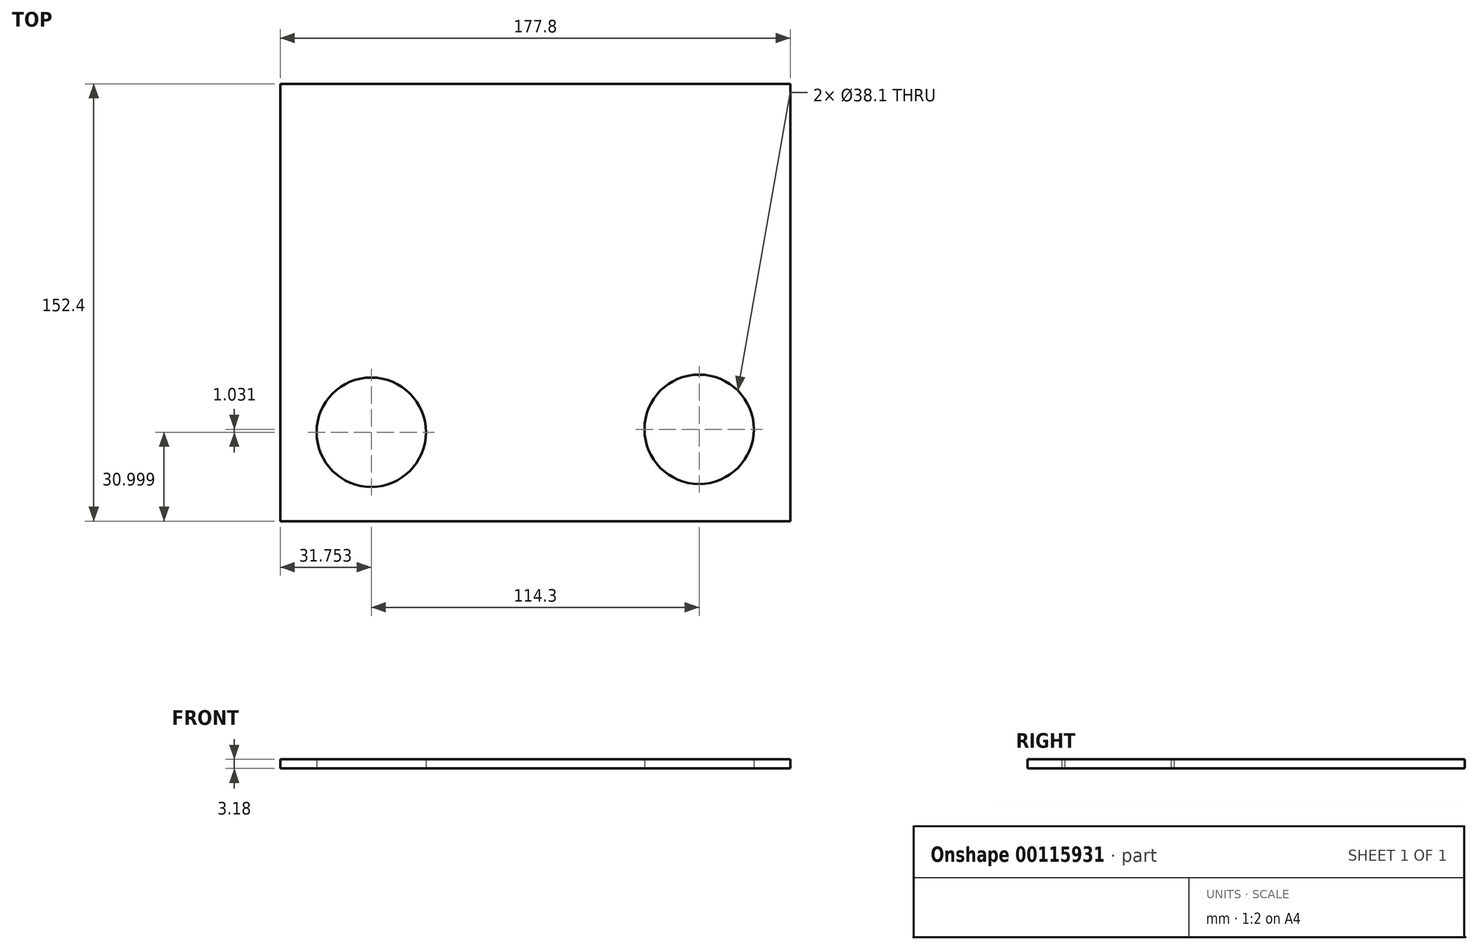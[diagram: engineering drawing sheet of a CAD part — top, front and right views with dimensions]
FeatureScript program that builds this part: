
annotation { "Feature Type Name" : "Feature", "Feature Type Description" : "" }
export const myFeature = defineFeature(function(context is Context, id is Id, definition is map)
    precondition{}
    {
        {
            var Q0;
            Q0=qCreatedBy(makeId("Top.planeOp"),FACE);
            var sketch = newSketch(context, id + "F0", { "sketchPlane" : qUnion([Q0])});
            skLineSegment(sketch, "E0.bottom", {"start": v(-98.76, 74.64) * mm, "end": v(79.04, 74.64) * mm});
            skLineSegment(sketch, "E0.top", {"start": v(-98.76, -77.76) * mm, "end": v(79.04, -77.76) * mm});
            skLineSegment(sketch, "E0.left", {"start": v(-98.76, 74.64) * mm, "end": v(-98.76, -77.76) * mm});
            skLineSegment(sketch, "E0.right", {"start": v(79.04, 74.64) * mm, "end": v(79.04, -77.76) * mm});
            skCircle(sketch, "E1", {"center": v(-67, -46.76) * mm, "radius": 19.05 * mm});
            skCircle(sketch, "E2", {"center": v(47.3, -45.73) * mm, "radius": 19.05 * mm});
            skSolve(sketch);
        }
        {
            var Q0;
            Q0=makeQuery(id+"F0.imprint","IMPRINT",FACE,{"disambiguationData":[TD([[makeQuery(id+"F0.imprint","IMPRINT",EDGE,{"derivedFrom":sQuery(id+"F0.wireOp",EDGE,"E0.bottom")}),-1.0]])]});
            extrude(context, id + "F1", {"entities" : qUnion([Q0]), "depth" : 3.17 * mm});
        }
    });
